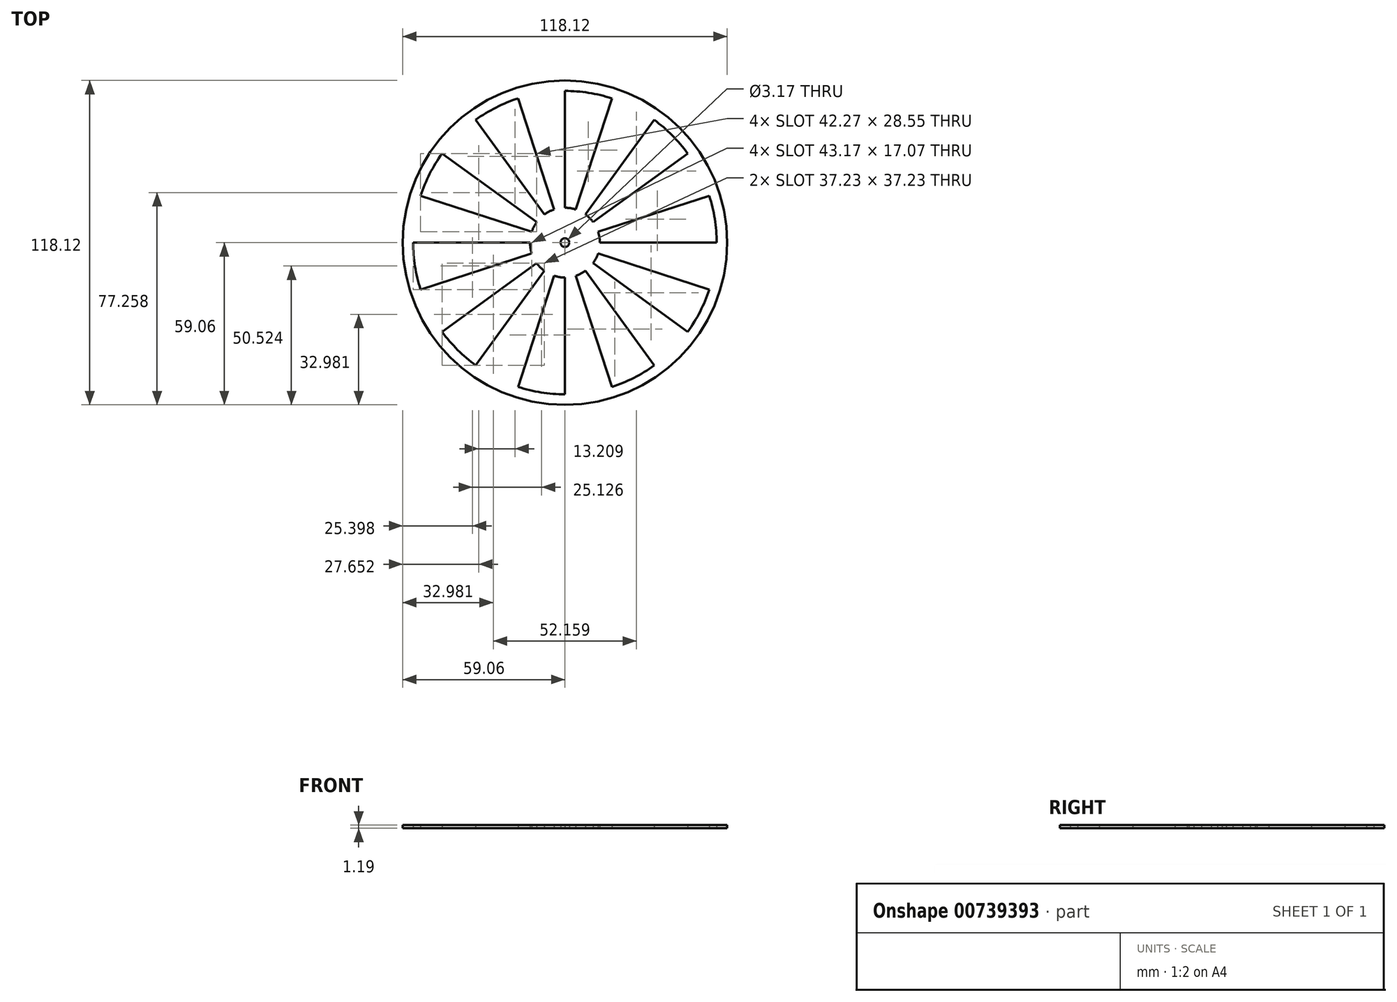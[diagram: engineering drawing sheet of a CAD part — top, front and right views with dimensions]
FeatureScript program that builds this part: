
annotation { "Feature Type Name" : "Feature", "Feature Type Description" : "" }
export const myFeature = defineFeature(function(context is Context, id is Id, definition is map)
    precondition{}
    {
        {
            var Q0;
            Q0=qCreatedBy(makeId("Top.planeOp"),FACE);
            var sketch = newSketch(context, id + "F0", { "sketchPlane" : qUnion([Q0])});
            skCircle(sketch, "E0", {"center": v(0, 0) * mm, "radius": 59.06 * mm});
            skCircle(sketch, "E1", {"center": v(0, 0) * mm, "radius": 55.25 * mm});
            skLineSegment(sketch, "E2", {"start": v(0, 0) * mm, "end": v(0, 55.25) * mm});
            skLineSegment(sketch, "E3", {"start": v(0, 0) * mm, "end": v(17.07, 52.54) * mm});
            skLineSegment(sketch, "E4", {"start": v(0, 0) * mm, "end": v(32.47, 44.7) * mm});
            skLineSegment(sketch, "E5", {"start": v(0, 0) * mm, "end": v(44.7, 32.47) * mm});
            skLineSegment(sketch, "E6", {"start": v(0, 0) * mm, "end": v(52.54, 17.07) * mm});
            skLineSegment(sketch, "E7", {"start": v(0, 0) * mm, "end": v(55.25, 0) * mm});
            skLineSegment(sketch, "E8", {"start": v(0, 0) * mm, "end": v(-17.07, 52.54) * mm});
            skLineSegment(sketch, "E9", {"start": v(0, 0) * mm, "end": v(-32.47, 44.7) * mm});
            skLineSegment(sketch, "E10", {"start": v(0, 0) * mm, "end": v(-44.7, 32.47) * mm});
            skLineSegment(sketch, "E11", {"start": v(0, 0) * mm, "end": v(-52.54, 17.07) * mm});
            skLineSegment(sketch, "E12", {"start": v(-55.25, 0) * mm, "end": v(0, 0) * mm});
            skLineSegment(sketch, "E13", {"start": v(0, 0) * mm, "end": v(-52.54, -17.07) * mm});
            skLineSegment(sketch, "E14", {"start": v(0, 0) * mm, "end": v(-44.7, -32.47) * mm});
            skLineSegment(sketch, "E15", {"start": v(0, 0) * mm, "end": v(-32.47, -44.7) * mm});
            skLineSegment(sketch, "E16", {"start": v(0, 0) * mm, "end": v(-17.07, -52.54) * mm});
            skLineSegment(sketch, "E17", {"start": v(0, 0) * mm, "end": v(0, -55.25) * mm});
            skLineSegment(sketch, "E18", {"start": v(0, 0) * mm, "end": v(17.07, -52.54) * mm});
            skLineSegment(sketch, "E19", {"start": v(0, 0) * mm, "end": v(32.47, -44.7) * mm});
            skLineSegment(sketch, "E20", {"start": v(0, 0) * mm, "end": v(44.7, -32.47) * mm});
            skLineSegment(sketch, "E21", {"start": v(0, 0) * mm, "end": v(52.54, -17.07) * mm});
            skCircle(sketch, "E22", {"center": v(0, 0) * mm, "radius": 12.7 * mm});
            skCircle(sketch, "E23", {"center": v(0, 0) * mm, "radius": 1.59 * mm});
            skSolve(sketch);
        }
        {
            var Q0;
            Q0=makeQuery(id+"F0.imprint","IMPRINT",FACE,{"disambiguationData":[TD([[makeQuery(id+"F0.imprint","IMPRINT",EDGE,{"derivedFrom":sQuery(id+"F0.wireOp",EDGE,"E0")}),1.0]])]});
            var Q1;
            {var subQ0=sQuery(id+"F0.wireOp",EDGE,"E17");var subQ1=sQuery(id+"F0.wireOp",EDGE,"E1");var subQ2=makeQuery(id+"F0.imprint","INTERSECT",VERTEX,{"derivedFrom":[subQ1,subQ0]});Q1=makeQuery(id+"F0.imprint","IMPRINT",FACE,{"disambiguationData":[TD([[makeQuery(id+"F0.imprint","IMPRINT",EDGE,{"disambiguationData":[TD([[subQ2,-1.0]])],"derivedFrom":subQ1}),1.0]])]});}
            var Q2;
            {var subQ0=sQuery(id+"F0.wireOp",EDGE,"E15");var subQ1=sQuery(id+"F0.wireOp",EDGE,"E1");var subQ2=makeQuery(id+"F0.imprint","INTERSECT",VERTEX,{"derivedFrom":[subQ1,subQ0]});Q2=makeQuery(id+"F0.imprint","IMPRINT",FACE,{"disambiguationData":[TD([[makeQuery(id+"F0.imprint","IMPRINT",EDGE,{"disambiguationData":[TD([[subQ2,-1.0]])],"derivedFrom":subQ1}),1.0]])]});}
            var Q3;
            {var subQ0=sQuery(id+"F0.wireOp",EDGE,"E13");var subQ1=sQuery(id+"F0.wireOp",EDGE,"E1");var subQ2=makeQuery(id+"F0.imprint","INTERSECT",VERTEX,{"derivedFrom":[subQ1,subQ0]});Q3=makeQuery(id+"F0.imprint","IMPRINT",FACE,{"disambiguationData":[TD([[makeQuery(id+"F0.imprint","IMPRINT",EDGE,{"disambiguationData":[TD([[subQ2,-1.0]])],"derivedFrom":subQ1}),1.0]])]});}
            var Q4;
            {var subQ0=sQuery(id+"F0.wireOp",EDGE,"E11");var subQ1=sQuery(id+"F0.wireOp",EDGE,"E1");var subQ2=makeQuery(id+"F0.imprint","INTERSECT",VERTEX,{"derivedFrom":[subQ1,subQ0]});Q4=makeQuery(id+"F0.imprint","IMPRINT",FACE,{"disambiguationData":[TD([[makeQuery(id+"F0.imprint","IMPRINT",EDGE,{"disambiguationData":[TD([[subQ2,-1.0]])],"derivedFrom":subQ1}),1.0]])]});}
            var Q5;
            {var subQ0=sQuery(id+"F0.wireOp",EDGE,"E9");var subQ1=sQuery(id+"F0.wireOp",EDGE,"E1");var subQ2=makeQuery(id+"F0.imprint","INTERSECT",VERTEX,{"derivedFrom":[subQ1,subQ0]});Q5=makeQuery(id+"F0.imprint","IMPRINT",FACE,{"disambiguationData":[TD([[makeQuery(id+"F0.imprint","IMPRINT",EDGE,{"disambiguationData":[TD([[subQ2,-1.0]])],"derivedFrom":subQ1}),1.0]])]});}
            var Q6;
            {var subQ0=sQuery(id+"F0.wireOp",EDGE,"E2");var subQ1=sQuery(id+"F0.wireOp",EDGE,"E1");var subQ2=makeQuery(id+"F0.imprint","INTERSECT",VERTEX,{"derivedFrom":[subQ1,subQ0]});Q6=makeQuery(id+"F0.imprint","IMPRINT",FACE,{"disambiguationData":[TD([[makeQuery(id+"F0.imprint","IMPRINT",EDGE,{"disambiguationData":[TD([[subQ2,-1.0]])],"derivedFrom":subQ1}),1.0]])]});}
            var Q7;
            {var subQ0=sQuery(id+"F0.wireOp",EDGE,"E3");var subQ1=sQuery(id+"F0.wireOp",EDGE,"E1");var subQ2=makeQuery(id+"F0.imprint","INTERSECT",VERTEX,{"derivedFrom":[subQ1,subQ0]});Q7=makeQuery(id+"F0.imprint","IMPRINT",FACE,{"disambiguationData":[TD([[makeQuery(id+"F0.imprint","IMPRINT",EDGE,{"disambiguationData":[TD([[subQ2,1.0]])],"derivedFrom":subQ1}),1.0]])]});}
            var Q8;
            {var subQ0=sQuery(id+"F0.wireOp",EDGE,"E5");var subQ1=sQuery(id+"F0.wireOp",EDGE,"E1");var subQ2=makeQuery(id+"F0.imprint","INTERSECT",VERTEX,{"derivedFrom":[subQ1,subQ0]});Q8=makeQuery(id+"F0.imprint","IMPRINT",FACE,{"disambiguationData":[TD([[makeQuery(id+"F0.imprint","IMPRINT",EDGE,{"disambiguationData":[TD([[subQ2,1.0]])],"derivedFrom":subQ1}),1.0]])]});}
            var Q9;
            {var subQ0=sQuery(id+"F0.wireOp",EDGE,"E7");var subQ1=sQuery(id+"F0.wireOp",EDGE,"E1");var subQ2=makeQuery(id+"F0.imprint","INTERSECT",VERTEX,{"derivedFrom":[subQ1,subQ0]});Q9=makeQuery(id+"F0.imprint","IMPRINT",FACE,{"disambiguationData":[TD([[makeQuery(id+"F0.imprint","IMPRINT",EDGE,{"disambiguationData":[TD([[subQ2,1.0]])],"derivedFrom":subQ1}),1.0]])]});}
            var Q10;
            {var subQ0=sQuery(id+"F0.wireOp",EDGE,"E19");var subQ1=sQuery(id+"F0.wireOp",EDGE,"E1");var subQ2=makeQuery(id+"F0.imprint","INTERSECT",VERTEX,{"derivedFrom":[subQ1,subQ0]});Q10=makeQuery(id+"F0.imprint","IMPRINT",FACE,{"disambiguationData":[TD([[makeQuery(id+"F0.imprint","IMPRINT",EDGE,{"disambiguationData":[TD([[subQ2,-1.0]])],"derivedFrom":subQ1}),1.0]])]});}
            var Q11;
            {var subQ1=sQuery(id+"F0.wireOp",EDGE,"E2");var subQ3=sQuery(id+"F0.wireOp",EDGE,"E22");var subQ4=makeQuery(id+"F0.imprint","INTERSECT",VERTEX,{"derivedFrom":[subQ1,subQ3]});Q11=makeQuery(id+"F0.imprint","IMPRINT",FACE,{"disambiguationData":[TD([[makeQuery(id+"F0.imprint","IMPRINT",EDGE,{"disambiguationData":[TD([[subQ4,1.0]])],"derivedFrom":subQ3}),1.0]])]});}
            var Q12;
            {var subQ1=sQuery(id+"F0.wireOp",EDGE,"E2");var subQ3=sQuery(id+"F0.wireOp",EDGE,"E22");var subQ4=makeQuery(id+"F0.imprint","INTERSECT",VERTEX,{"derivedFrom":[subQ1,subQ3]});Q12=makeQuery(id+"F0.imprint","IMPRINT",FACE,{"disambiguationData":[TD([[makeQuery(id+"F0.imprint","IMPRINT",EDGE,{"disambiguationData":[TD([[subQ4,-1.0]])],"derivedFrom":subQ3}),1.0]])]});}
            var Q13;
            {var subQ1=sQuery(id+"F0.wireOp",EDGE,"E8");var subQ3=sQuery(id+"F0.wireOp",EDGE,"E22");var subQ4=makeQuery(id+"F0.imprint","INTERSECT",VERTEX,{"derivedFrom":[subQ1,subQ3]});Q13=makeQuery(id+"F0.imprint","IMPRINT",FACE,{"disambiguationData":[TD([[makeQuery(id+"F0.imprint","IMPRINT",EDGE,{"disambiguationData":[TD([[subQ4,-1.0]])],"derivedFrom":subQ3}),1.0]])]});}
            var Q14;
            {var subQ1=sQuery(id+"F0.wireOp",EDGE,"E9");var subQ3=sQuery(id+"F0.wireOp",EDGE,"E22");var subQ4=makeQuery(id+"F0.imprint","INTERSECT",VERTEX,{"derivedFrom":[subQ1,subQ3]});Q14=makeQuery(id+"F0.imprint","IMPRINT",FACE,{"disambiguationData":[TD([[makeQuery(id+"F0.imprint","IMPRINT",EDGE,{"disambiguationData":[TD([[subQ4,-1.0]])],"derivedFrom":subQ3}),1.0]])]});}
            var Q15;
            {var subQ1=sQuery(id+"F0.wireOp",EDGE,"E10");var subQ3=sQuery(id+"F0.wireOp",EDGE,"E22");var subQ4=makeQuery(id+"F0.imprint","INTERSECT",VERTEX,{"derivedFrom":[subQ1,subQ3]});Q15=makeQuery(id+"F0.imprint","IMPRINT",FACE,{"disambiguationData":[TD([[makeQuery(id+"F0.imprint","IMPRINT",EDGE,{"disambiguationData":[TD([[subQ4,-1.0]])],"derivedFrom":subQ3}),1.0]])]});}
            var Q16;
            {var subQ1=sQuery(id+"F0.wireOp",EDGE,"E11");var subQ3=sQuery(id+"F0.wireOp",EDGE,"E22");var subQ4=makeQuery(id+"F0.imprint","INTERSECT",VERTEX,{"derivedFrom":[subQ1,subQ3]});Q16=makeQuery(id+"F0.imprint","IMPRINT",FACE,{"disambiguationData":[TD([[makeQuery(id+"F0.imprint","IMPRINT",EDGE,{"disambiguationData":[TD([[subQ4,-1.0]])],"derivedFrom":subQ3}),1.0]])]});}
            var Q17;
            {var subQ1=sQuery(id+"F0.wireOp",EDGE,"E12");var subQ3=sQuery(id+"F0.wireOp",EDGE,"E22");var subQ4=makeQuery(id+"F0.imprint","INTERSECT",VERTEX,{"derivedFrom":[subQ1,subQ3]});Q17=makeQuery(id+"F0.imprint","IMPRINT",FACE,{"disambiguationData":[TD([[makeQuery(id+"F0.imprint","IMPRINT",EDGE,{"disambiguationData":[TD([[subQ4,-1.0]])],"derivedFrom":subQ3}),1.0]])]});}
            var Q18;
            {var subQ1=sQuery(id+"F0.wireOp",EDGE,"E13");var subQ3=sQuery(id+"F0.wireOp",EDGE,"E22");var subQ4=makeQuery(id+"F0.imprint","INTERSECT",VERTEX,{"derivedFrom":[subQ1,subQ3]});Q18=makeQuery(id+"F0.imprint","IMPRINT",FACE,{"disambiguationData":[TD([[makeQuery(id+"F0.imprint","IMPRINT",EDGE,{"disambiguationData":[TD([[subQ4,-1.0]])],"derivedFrom":subQ3}),1.0]])]});}
            var Q19;
            {var subQ1=sQuery(id+"F0.wireOp",EDGE,"E14");var subQ3=sQuery(id+"F0.wireOp",EDGE,"E22");var subQ4=makeQuery(id+"F0.imprint","INTERSECT",VERTEX,{"derivedFrom":[subQ1,subQ3]});Q19=makeQuery(id+"F0.imprint","IMPRINT",FACE,{"disambiguationData":[TD([[makeQuery(id+"F0.imprint","IMPRINT",EDGE,{"disambiguationData":[TD([[subQ4,-1.0]])],"derivedFrom":subQ3}),1.0]])]});}
            var Q20;
            {var subQ1=sQuery(id+"F0.wireOp",EDGE,"E15");var subQ3=sQuery(id+"F0.wireOp",EDGE,"E22");var subQ4=makeQuery(id+"F0.imprint","INTERSECT",VERTEX,{"derivedFrom":[subQ1,subQ3]});Q20=makeQuery(id+"F0.imprint","IMPRINT",FACE,{"disambiguationData":[TD([[makeQuery(id+"F0.imprint","IMPRINT",EDGE,{"disambiguationData":[TD([[subQ4,-1.0]])],"derivedFrom":subQ3}),1.0]])]});}
            var Q21;
            {var subQ1=sQuery(id+"F0.wireOp",EDGE,"E16");var subQ3=sQuery(id+"F0.wireOp",EDGE,"E22");var subQ4=makeQuery(id+"F0.imprint","INTERSECT",VERTEX,{"derivedFrom":[subQ1,subQ3]});Q21=makeQuery(id+"F0.imprint","IMPRINT",FACE,{"disambiguationData":[TD([[makeQuery(id+"F0.imprint","IMPRINT",EDGE,{"disambiguationData":[TD([[subQ4,-1.0]])],"derivedFrom":subQ3}),1.0]])]});}
            var Q22;
            {var subQ1=sQuery(id+"F0.wireOp",EDGE,"E17");var subQ3=sQuery(id+"F0.wireOp",EDGE,"E22");var subQ4=makeQuery(id+"F0.imprint","INTERSECT",VERTEX,{"derivedFrom":[subQ1,subQ3]});Q22=makeQuery(id+"F0.imprint","IMPRINT",FACE,{"disambiguationData":[TD([[makeQuery(id+"F0.imprint","IMPRINT",EDGE,{"disambiguationData":[TD([[subQ4,-1.0]])],"derivedFrom":subQ3}),1.0]])]});}
            var Q23;
            {var subQ1=sQuery(id+"F0.wireOp",EDGE,"E18");var subQ3=sQuery(id+"F0.wireOp",EDGE,"E22");var subQ4=makeQuery(id+"F0.imprint","INTERSECT",VERTEX,{"derivedFrom":[subQ1,subQ3]});Q23=makeQuery(id+"F0.imprint","IMPRINT",FACE,{"disambiguationData":[TD([[makeQuery(id+"F0.imprint","IMPRINT",EDGE,{"disambiguationData":[TD([[subQ4,-1.0]])],"derivedFrom":subQ3}),1.0]])]});}
            var Q24;
            {var subQ1=sQuery(id+"F0.wireOp",EDGE,"E19");var subQ3=sQuery(id+"F0.wireOp",EDGE,"E22");var subQ4=makeQuery(id+"F0.imprint","INTERSECT",VERTEX,{"derivedFrom":[subQ1,subQ3]});Q24=makeQuery(id+"F0.imprint","IMPRINT",FACE,{"disambiguationData":[TD([[makeQuery(id+"F0.imprint","IMPRINT",EDGE,{"disambiguationData":[TD([[subQ4,-1.0]])],"derivedFrom":subQ3}),1.0]])]});}
            var Q25;
            {var subQ1=sQuery(id+"F0.wireOp",EDGE,"E20");var subQ3=sQuery(id+"F0.wireOp",EDGE,"E22");var subQ4=makeQuery(id+"F0.imprint","INTERSECT",VERTEX,{"derivedFrom":[subQ1,subQ3]});Q25=makeQuery(id+"F0.imprint","IMPRINT",FACE,{"disambiguationData":[TD([[makeQuery(id+"F0.imprint","IMPRINT",EDGE,{"disambiguationData":[TD([[subQ4,-1.0]])],"derivedFrom":subQ3}),1.0]])]});}
            var Q26;
            {var subQ1=sQuery(id+"F0.wireOp",EDGE,"E7");var subQ3=sQuery(id+"F0.wireOp",EDGE,"E22");var subQ4=makeQuery(id+"F0.imprint","INTERSECT",VERTEX,{"derivedFrom":[subQ1,subQ3]});Q26=makeQuery(id+"F0.imprint","IMPRINT",FACE,{"disambiguationData":[TD([[makeQuery(id+"F0.imprint","IMPRINT",EDGE,{"disambiguationData":[TD([[subQ4,1.0]])],"derivedFrom":subQ3}),1.0]])]});}
            var Q27;
            {var subQ1=sQuery(id+"F0.wireOp",EDGE,"E6");var subQ3=sQuery(id+"F0.wireOp",EDGE,"E22");var subQ4=makeQuery(id+"F0.imprint","INTERSECT",VERTEX,{"derivedFrom":[subQ1,subQ3]});Q27=makeQuery(id+"F0.imprint","IMPRINT",FACE,{"disambiguationData":[TD([[makeQuery(id+"F0.imprint","IMPRINT",EDGE,{"disambiguationData":[TD([[subQ4,1.0]])],"derivedFrom":subQ3}),1.0]])]});}
            var Q28;
            {var subQ1=sQuery(id+"F0.wireOp",EDGE,"E5");var subQ3=sQuery(id+"F0.wireOp",EDGE,"E22");var subQ4=makeQuery(id+"F0.imprint","INTERSECT",VERTEX,{"derivedFrom":[subQ1,subQ3]});Q28=makeQuery(id+"F0.imprint","IMPRINT",FACE,{"disambiguationData":[TD([[makeQuery(id+"F0.imprint","IMPRINT",EDGE,{"disambiguationData":[TD([[subQ4,1.0]])],"derivedFrom":subQ3}),1.0]])]});}
            var Q29;
            {var subQ1=sQuery(id+"F0.wireOp",EDGE,"E4");var subQ3=sQuery(id+"F0.wireOp",EDGE,"E22");var subQ4=makeQuery(id+"F0.imprint","INTERSECT",VERTEX,{"derivedFrom":[subQ1,subQ3]});Q29=makeQuery(id+"F0.imprint","IMPRINT",FACE,{"disambiguationData":[TD([[makeQuery(id+"F0.imprint","IMPRINT",EDGE,{"disambiguationData":[TD([[subQ4,1.0]])],"derivedFrom":subQ3}),1.0]])]});}
            var Q30;
            {var subQ1=sQuery(id+"F0.wireOp",EDGE,"E3");var subQ3=sQuery(id+"F0.wireOp",EDGE,"E22");var subQ4=makeQuery(id+"F0.imprint","INTERSECT",VERTEX,{"derivedFrom":[subQ1,subQ3]});Q30=makeQuery(id+"F0.imprint","IMPRINT",FACE,{"disambiguationData":[TD([[makeQuery(id+"F0.imprint","IMPRINT",EDGE,{"disambiguationData":[TD([[subQ4,1.0]])],"derivedFrom":subQ3}),1.0]])]});}
            extrude(context, id + "F1", {"entities" : qUnion([Q0, Q1, Q2, Q3, Q4, Q5, Q6, Q7, Q8, Q9, Q10, Q11, Q12, Q13, Q14, Q15, Q16, Q17, Q18, Q19, Q20, Q21, Q22, Q23, Q24, Q25, Q26, Q27, Q28, Q29, Q30]), "depth" : 1.2 * mm, "offsetDistance" : 25.4 * mm});
        }
        {
            var Q0;
            {var subQ1=sQuery(id+"F0.wireOp",EDGE,"E14");var subQ3=sQuery(id+"F0.wireOp",EDGE,"E23");var subQ4=makeQuery(id+"F0.imprint","INTERSECT",VERTEX,{"derivedFrom":[subQ1,subQ3]});Q0=makeQuery(id+"F0.imprint","IMPRINT",FACE,{"disambiguationData":[TD([[makeQuery(id+"F0.imprint","IMPRINT",EDGE,{"disambiguationData":[TD([[subQ4,-1.0]])],"derivedFrom":subQ3}),1.0]])]});}
            var Q1;
            {var subQ1=sQuery(id+"F0.wireOp",EDGE,"E13");var subQ3=sQuery(id+"F0.wireOp",EDGE,"E23");var subQ4=makeQuery(id+"F0.imprint","INTERSECT",VERTEX,{"derivedFrom":[subQ1,subQ3]});Q1=makeQuery(id+"F0.imprint","IMPRINT",FACE,{"disambiguationData":[TD([[makeQuery(id+"F0.imprint","IMPRINT",EDGE,{"disambiguationData":[TD([[subQ4,-1.0]])],"derivedFrom":subQ3}),1.0]])]});}
            var Q2;
            {var subQ1=sQuery(id+"F0.wireOp",EDGE,"E12");var subQ3=sQuery(id+"F0.wireOp",EDGE,"E23");var subQ4=makeQuery(id+"F0.imprint","INTERSECT",VERTEX,{"derivedFrom":[subQ1,subQ3]});Q2=makeQuery(id+"F0.imprint","IMPRINT",FACE,{"disambiguationData":[TD([[makeQuery(id+"F0.imprint","IMPRINT",EDGE,{"disambiguationData":[TD([[subQ4,-1.0]])],"derivedFrom":subQ3}),1.0]])]});}
            var Q3;
            {var subQ1=sQuery(id+"F0.wireOp",EDGE,"E11");var subQ3=sQuery(id+"F0.wireOp",EDGE,"E23");var subQ4=makeQuery(id+"F0.imprint","INTERSECT",VERTEX,{"derivedFrom":[subQ1,subQ3]});Q3=makeQuery(id+"F0.imprint","IMPRINT",FACE,{"disambiguationData":[TD([[makeQuery(id+"F0.imprint","IMPRINT",EDGE,{"disambiguationData":[TD([[subQ4,-1.0]])],"derivedFrom":subQ3}),1.0]])]});}
            var Q4;
            {var subQ1=sQuery(id+"F0.wireOp",EDGE,"E10");var subQ3=sQuery(id+"F0.wireOp",EDGE,"E23");var subQ4=makeQuery(id+"F0.imprint","INTERSECT",VERTEX,{"derivedFrom":[subQ1,subQ3]});Q4=makeQuery(id+"F0.imprint","IMPRINT",FACE,{"disambiguationData":[TD([[makeQuery(id+"F0.imprint","IMPRINT",EDGE,{"disambiguationData":[TD([[subQ4,-1.0]])],"derivedFrom":subQ3}),1.0]])]});}
            var Q5;
            {var subQ1=sQuery(id+"F0.wireOp",EDGE,"E9");var subQ3=sQuery(id+"F0.wireOp",EDGE,"E23");var subQ4=makeQuery(id+"F0.imprint","INTERSECT",VERTEX,{"derivedFrom":[subQ1,subQ3]});Q5=makeQuery(id+"F0.imprint","IMPRINT",FACE,{"disambiguationData":[TD([[makeQuery(id+"F0.imprint","IMPRINT",EDGE,{"disambiguationData":[TD([[subQ4,-1.0]])],"derivedFrom":subQ3}),1.0]])]});}
            var Q6;
            {var subQ1=sQuery(id+"F0.wireOp",EDGE,"E8");var subQ3=sQuery(id+"F0.wireOp",EDGE,"E23");var subQ4=makeQuery(id+"F0.imprint","INTERSECT",VERTEX,{"derivedFrom":[subQ1,subQ3]});Q6=makeQuery(id+"F0.imprint","IMPRINT",FACE,{"disambiguationData":[TD([[makeQuery(id+"F0.imprint","IMPRINT",EDGE,{"disambiguationData":[TD([[subQ4,-1.0]])],"derivedFrom":subQ3}),1.0]])]});}
            var Q7;
            {var subQ1=sQuery(id+"F0.wireOp",EDGE,"E2");var subQ3=sQuery(id+"F0.wireOp",EDGE,"E23");var subQ4=makeQuery(id+"F0.imprint","INTERSECT",VERTEX,{"derivedFrom":[subQ1,subQ3]});Q7=makeQuery(id+"F0.imprint","IMPRINT",FACE,{"disambiguationData":[TD([[makeQuery(id+"F0.imprint","IMPRINT",EDGE,{"disambiguationData":[TD([[subQ4,-1.0]])],"derivedFrom":subQ3}),1.0]])]});}
            var Q8;
            {var subQ1=sQuery(id+"F0.wireOp",EDGE,"E2");var subQ3=sQuery(id+"F0.wireOp",EDGE,"E23");var subQ4=makeQuery(id+"F0.imprint","INTERSECT",VERTEX,{"derivedFrom":[subQ1,subQ3]});Q8=makeQuery(id+"F0.imprint","IMPRINT",FACE,{"disambiguationData":[TD([[makeQuery(id+"F0.imprint","IMPRINT",EDGE,{"disambiguationData":[TD([[subQ4,1.0]])],"derivedFrom":subQ3}),1.0]])]});}
            var Q9;
            {var subQ1=sQuery(id+"F0.wireOp",EDGE,"E3");var subQ3=sQuery(id+"F0.wireOp",EDGE,"E23");var subQ4=makeQuery(id+"F0.imprint","INTERSECT",VERTEX,{"derivedFrom":[subQ1,subQ3]});Q9=makeQuery(id+"F0.imprint","IMPRINT",FACE,{"disambiguationData":[TD([[makeQuery(id+"F0.imprint","IMPRINT",EDGE,{"disambiguationData":[TD([[subQ4,1.0]])],"derivedFrom":subQ3}),1.0]])]});}
            var Q10;
            {var subQ1=sQuery(id+"F0.wireOp",EDGE,"E4");var subQ3=sQuery(id+"F0.wireOp",EDGE,"E23");var subQ4=makeQuery(id+"F0.imprint","INTERSECT",VERTEX,{"derivedFrom":[subQ1,subQ3]});Q10=makeQuery(id+"F0.imprint","IMPRINT",FACE,{"disambiguationData":[TD([[makeQuery(id+"F0.imprint","IMPRINT",EDGE,{"disambiguationData":[TD([[subQ4,1.0]])],"derivedFrom":subQ3}),1.0]])]});}
            var Q11;
            {var subQ1=sQuery(id+"F0.wireOp",EDGE,"E5");var subQ3=sQuery(id+"F0.wireOp",EDGE,"E23");var subQ4=makeQuery(id+"F0.imprint","INTERSECT",VERTEX,{"derivedFrom":[subQ1,subQ3]});Q11=makeQuery(id+"F0.imprint","IMPRINT",FACE,{"disambiguationData":[TD([[makeQuery(id+"F0.imprint","IMPRINT",EDGE,{"disambiguationData":[TD([[subQ4,1.0]])],"derivedFrom":subQ3}),1.0]])]});}
            var Q12;
            {var subQ1=sQuery(id+"F0.wireOp",EDGE,"E6");var subQ3=sQuery(id+"F0.wireOp",EDGE,"E23");var subQ4=makeQuery(id+"F0.imprint","INTERSECT",VERTEX,{"derivedFrom":[subQ1,subQ3]});Q12=makeQuery(id+"F0.imprint","IMPRINT",FACE,{"disambiguationData":[TD([[makeQuery(id+"F0.imprint","IMPRINT",EDGE,{"disambiguationData":[TD([[subQ4,1.0]])],"derivedFrom":subQ3}),1.0]])]});}
            var Q13;
            {var subQ1=sQuery(id+"F0.wireOp",EDGE,"E7");var subQ3=sQuery(id+"F0.wireOp",EDGE,"E23");var subQ4=makeQuery(id+"F0.imprint","INTERSECT",VERTEX,{"derivedFrom":[subQ1,subQ3]});Q13=makeQuery(id+"F0.imprint","IMPRINT",FACE,{"disambiguationData":[TD([[makeQuery(id+"F0.imprint","IMPRINT",EDGE,{"disambiguationData":[TD([[subQ4,1.0]])],"derivedFrom":subQ3}),1.0]])]});}
            var Q14;
            {var subQ1=sQuery(id+"F0.wireOp",EDGE,"E20");var subQ3=sQuery(id+"F0.wireOp",EDGE,"E23");var subQ4=makeQuery(id+"F0.imprint","INTERSECT",VERTEX,{"derivedFrom":[subQ1,subQ3]});Q14=makeQuery(id+"F0.imprint","IMPRINT",FACE,{"disambiguationData":[TD([[makeQuery(id+"F0.imprint","IMPRINT",EDGE,{"disambiguationData":[TD([[subQ4,-1.0]])],"derivedFrom":subQ3}),1.0]])]});}
            var Q15;
            {var subQ1=sQuery(id+"F0.wireOp",EDGE,"E19");var subQ3=sQuery(id+"F0.wireOp",EDGE,"E23");var subQ4=makeQuery(id+"F0.imprint","INTERSECT",VERTEX,{"derivedFrom":[subQ1,subQ3]});Q15=makeQuery(id+"F0.imprint","IMPRINT",FACE,{"disambiguationData":[TD([[makeQuery(id+"F0.imprint","IMPRINT",EDGE,{"disambiguationData":[TD([[subQ4,-1.0]])],"derivedFrom":subQ3}),1.0]])]});}
            var Q16;
            {var subQ1=sQuery(id+"F0.wireOp",EDGE,"E18");var subQ3=sQuery(id+"F0.wireOp",EDGE,"E23");var subQ4=makeQuery(id+"F0.imprint","INTERSECT",VERTEX,{"derivedFrom":[subQ1,subQ3]});Q16=makeQuery(id+"F0.imprint","IMPRINT",FACE,{"disambiguationData":[TD([[makeQuery(id+"F0.imprint","IMPRINT",EDGE,{"disambiguationData":[TD([[subQ4,-1.0]])],"derivedFrom":subQ3}),1.0]])]});}
            var Q17;
            {var subQ1=sQuery(id+"F0.wireOp",EDGE,"E17");var subQ3=sQuery(id+"F0.wireOp",EDGE,"E23");var subQ4=makeQuery(id+"F0.imprint","INTERSECT",VERTEX,{"derivedFrom":[subQ1,subQ3]});Q17=makeQuery(id+"F0.imprint","IMPRINT",FACE,{"disambiguationData":[TD([[makeQuery(id+"F0.imprint","IMPRINT",EDGE,{"disambiguationData":[TD([[subQ4,-1.0]])],"derivedFrom":subQ3}),1.0]])]});}
            var Q18;
            {var subQ1=sQuery(id+"F0.wireOp",EDGE,"E16");var subQ3=sQuery(id+"F0.wireOp",EDGE,"E23");var subQ4=makeQuery(id+"F0.imprint","INTERSECT",VERTEX,{"derivedFrom":[subQ1,subQ3]});Q18=makeQuery(id+"F0.imprint","IMPRINT",FACE,{"disambiguationData":[TD([[makeQuery(id+"F0.imprint","IMPRINT",EDGE,{"disambiguationData":[TD([[subQ4,-1.0]])],"derivedFrom":subQ3}),1.0]])]});}
            var Q19;
            {var subQ1=sQuery(id+"F0.wireOp",EDGE,"E15");var subQ3=sQuery(id+"F0.wireOp",EDGE,"E23");var subQ4=makeQuery(id+"F0.imprint","INTERSECT",VERTEX,{"derivedFrom":[subQ1,subQ3]});Q19=makeQuery(id+"F0.imprint","IMPRINT",FACE,{"disambiguationData":[TD([[makeQuery(id+"F0.imprint","IMPRINT",EDGE,{"disambiguationData":[TD([[subQ4,-1.0]])],"derivedFrom":subQ3}),1.0]])]});}
            extrude(context, id + "F2", {"entities" : qUnion([Q0, Q1, Q2, Q3, Q4, Q5, Q6, Q7, Q8, Q9, Q10, Q11, Q12, Q13, Q14, Q15, Q16, Q17, Q18, Q19]), "operationType" : NewBodyOperationType.REMOVE, "oppositeDirection" : true, "depth" : 1.2 * mm, "offsetDistance" : 25.4 * mm});
        }
    });
